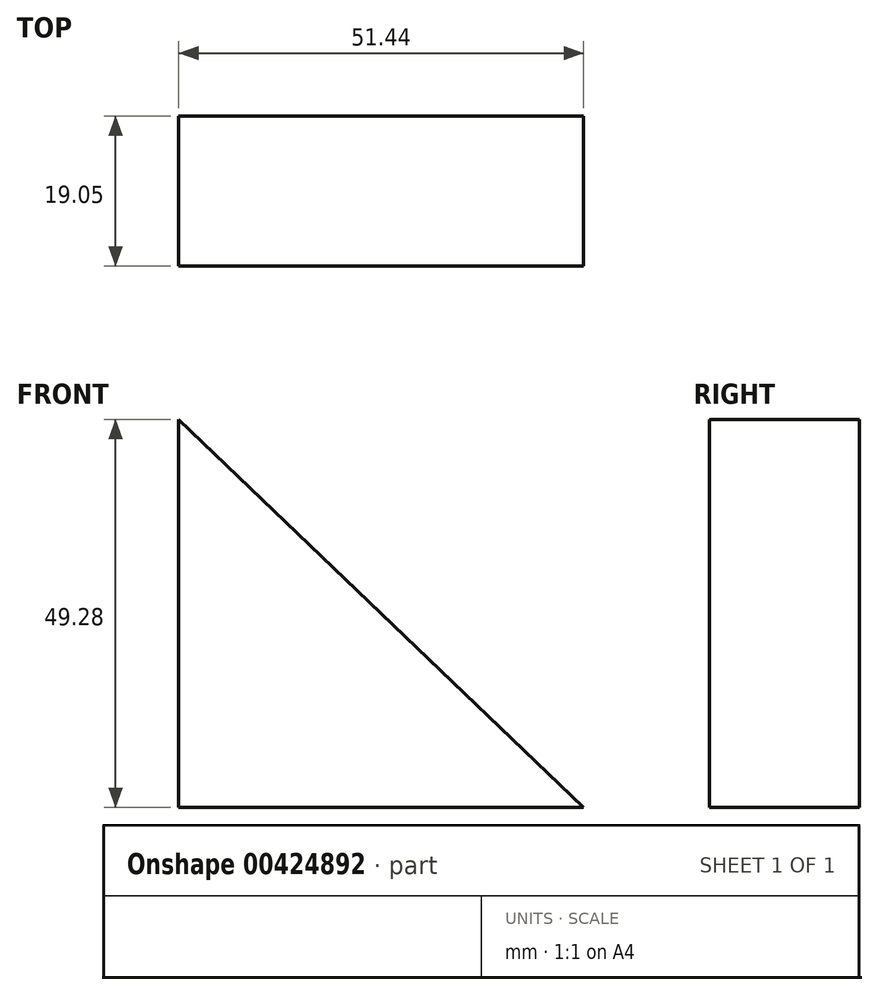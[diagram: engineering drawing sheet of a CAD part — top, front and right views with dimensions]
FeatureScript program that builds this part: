
annotation { "Feature Type Name" : "Feature", "Feature Type Description" : "" }
export const myFeature = defineFeature(function(context is Context, id is Id, definition is map)
    precondition{}
    {
        {
            var Q0;
            Q0=qCreatedBy(makeId("Front.planeOp"),FACE);
            var sketch = newSketch(context, id + "F0", { "sketchPlane" : qUnion([Q0])});
            skLineSegment(sketch, "E0", {"start": v(0, 0) * mm, "end": v(51.44, 0) * mm});
            skLineSegment(sketch, "E1", {"start": v(0, 0) * mm, "end": v(0, 49.28) * mm});
            skLineSegment(sketch, "E2", {"start": v(0, 49.28) * mm, "end": v(51.44, 0) * mm});
            skSolve(sketch);
        }
        {
            var Q0;
            Q0=makeQuery(id+"F0.imprint","IMPRINT",FACE,{"disambiguationData":[TD([[makeQuery(id+"F0.imprint","IMPRINT",EDGE,{"derivedFrom":sQuery(id+"F0.wireOp",EDGE,"E0")}),1.0]])]});
            var Q1;
            Q1 = qConstructionFilter(qBodyType(qCreatedBy(id + "F0" ,EDGE), BodyType.WIRE), ConstructionObject.NO);
            extrude(context, id + "F1", {"entities" : qUnion([Q0]), "surfaceEntities" : qUnion([Q1]), "depth" : 19.05 * mm});
        }
    });
